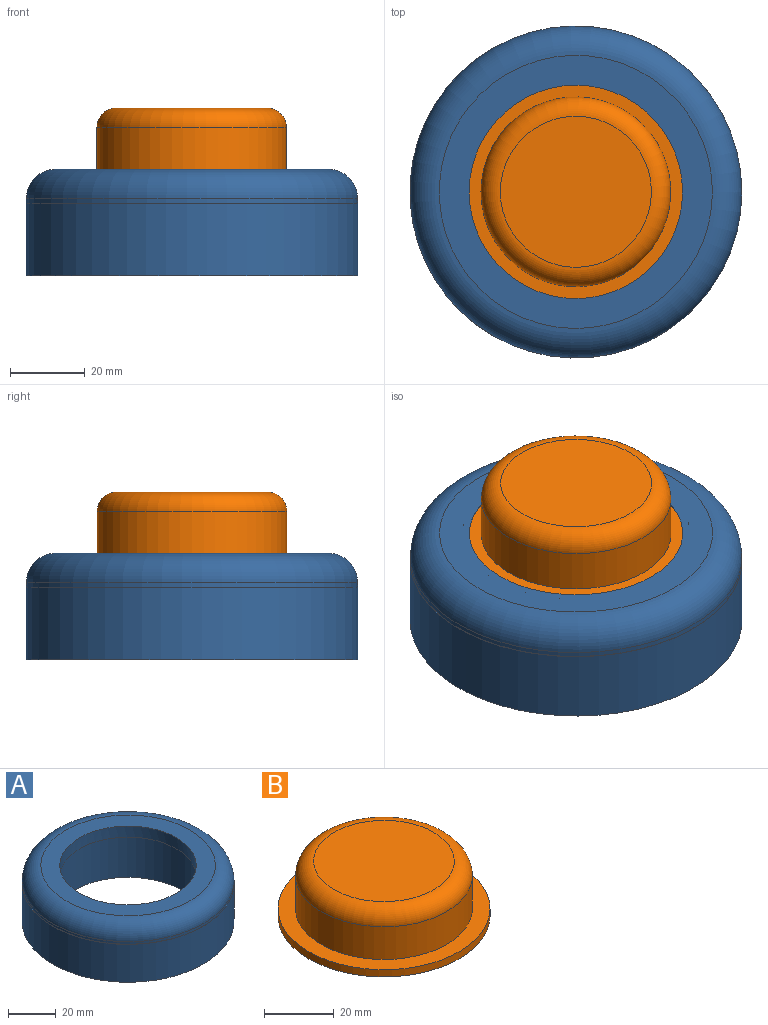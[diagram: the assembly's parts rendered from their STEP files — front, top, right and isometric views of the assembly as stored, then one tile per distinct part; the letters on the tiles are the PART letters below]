
ASSEMBLY  parts=2 mates=1
PART A: 9 faces, bbox 96x96x28.5 mm
  f0: cylinder r=44.45mm len=88.9mm, axis (0,0,-1), area 5433.9mm2, adj f1,f2
  f1: plane 88.9x88.9mm, normal (0,0,1), area 24.9mm2, adj f0,f3
  f2: plane 88.9x88.9mm, normal (0,0,-1), area 3040.2mm2, adj f0,f6
  f3: cylinder r=44.36mm len=88.72mm, axis (0,0,-1), area 361.1mm2, adj f1,f5
  f4: plane 73.13x73.13mm, normal (0,0,1), area 1634.6mm2, adj f5,f8
  f5: torus R=36.56mm, axis (0,0,1), area 3196mm2, adj f3,f4
  f6: cylinder r=31.75mm len=63.5mm, axis (0,0,-1), area 4560.4mm2, adj f2,f7
  f7: plane 63.5x63.5mm, normal (0,0,-1), area 601.7mm2, adj f6,f8
  f8: cylinder r=28.57mm len=57.15mm, axis (0,0,-1), area 1021.5mm2, adj f4,f7
PART B: 22 faces, bbox 61x61x19.3 mm
  f0: cylinder r=25.4mm len=50.8mm, axis (0,0,-1), area 1840.4mm2, adj f2,f5
  f1: plane 40.44x40.44mm, normal (0,0,1), area 1284.2mm2, adj f2
  f2: torus R=20.22mm, axis (0,0,1), area 1202.7mm2, adj f0,f1
  f3: cylinder r=30.48mm len=60.96mm, axis (0,0,1), area 486.4mm2, adj f4,f5
  f4: plane 60.96x60.96mm, normal (0,0,-1), area 2514.5mm2, adj f3,f6,f8,f10,f12,f14,f16,f18
  f5: plane 60.96x60.96mm, normal (0,0,1), area 891.8mm2, adj f0,f3
  f6: cylinder r=4.7mm len=10.16mm, axis (0,0,-1), area 300mm2, adj f4,f7
  f7: plane 9.4x9.4mm, normal (0,0,-1), area 69.4mm2, adj f6
  f8: cylinder r=3.17mm len=10.16mm, axis (0,0,-1), area 202.7mm2, adj f4,f9
  f9: plane 6.35x6.35mm, normal (0,0,-1), area 31.7mm2, adj f8
  f10: cylinder r=3.17mm len=10.16mm, axis (0,0,-1), area 202.7mm2, adj f4,f11
  f11: plane 6.35x6.35mm, normal (0,0,-1), area 31.7mm2, adj f10
  f12: cylinder r=3.17mm len=10.16mm, axis (0,0,-1), area 202.7mm2, adj f4,f13
  f13: plane 6.35x6.35mm, normal (0,0,-1), area 31.7mm2, adj f12
  f14: cylinder r=4.7mm len=10.16mm, axis (0,0,-1), area 300mm2, adj f4,f15
  f15: plane 9.4x9.4mm, normal (0,0,-1), area 69.4mm2, adj f14
  f16: cylinder r=4.7mm len=10.16mm, axis (0,0,-1), area 300mm2, adj f4,f17
  f17: plane 9.4x9.4mm, normal (0,0,-1), area 69.4mm2, adj f16
  f18: cylinder r=4.7mm len=10.16mm, axis (0,0,-1), area 300mm2, adj f4,f19
  f19: plane 9.4x9.4mm, normal (0,0,-1), area 69.4mm2, adj f18
  f20: cylinder r=3.17mm len=10.16mm, axis (0,0,-1), area 202.7mm2, adj f4,f21
  f21: plane 6.35x6.35mm, normal (0,0,-1), area 31.7mm2, adj f20
PLACE A rot(axis=(-0.22,0.95,0.21),0deg) t=(10.34,35.73,-15.94)mm
PLACE B rot(axis=(0,0,-1),180deg) t=(10.34,35.73,-8.63)mm
MATE slider B.f3 <-> A.f8  axis (0,0,-1) through (10.34,35.73,9.76)mm
